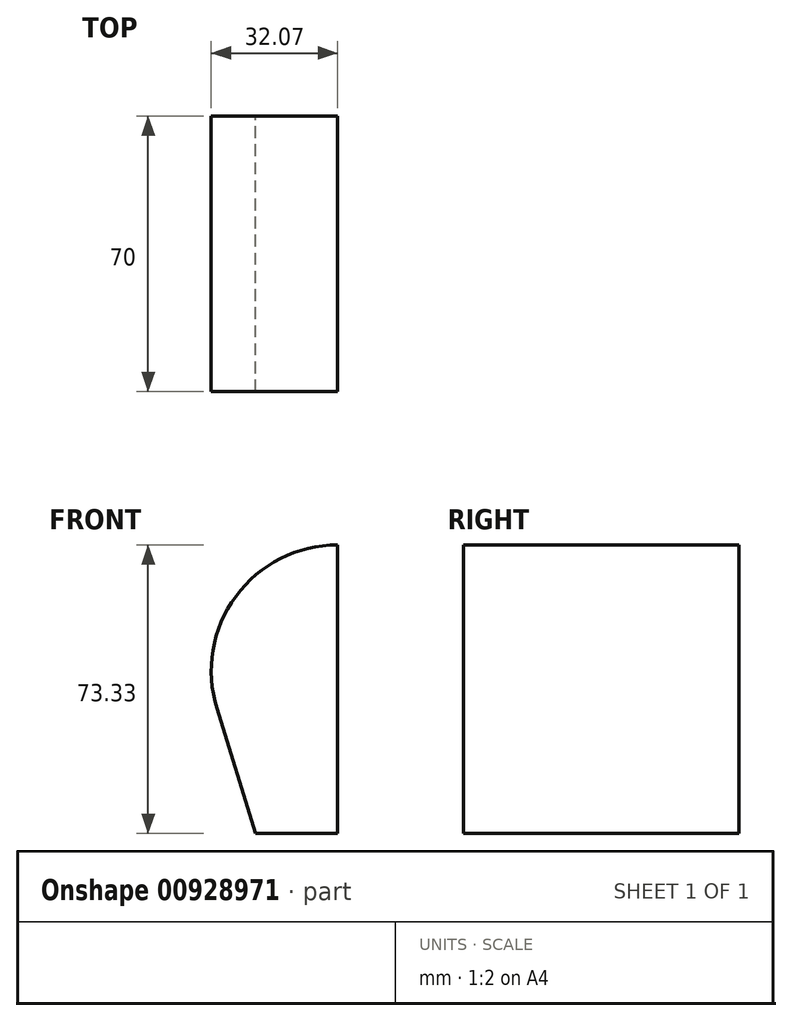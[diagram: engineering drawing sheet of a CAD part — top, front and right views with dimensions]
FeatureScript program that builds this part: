
annotation { "Feature Type Name" : "Feature", "Feature Type Description" : "" }
export const myFeature = defineFeature(function(context is Context, id is Id, definition is map)
    precondition{}
    {
        {
            var Q0;
            Q0=qCreatedBy(makeId("Front.planeOp"),FACE);
            var sketch = newSketch(context, id + "F0", { "sketchPlane" : qUnion([Q0])});
            skLineSegment(sketch, "E0", {"start": v(-16.44, -1.15) * mm, "end": v(-6.57, -32.89) * mm});
            skArc(sketch, "E1", {"start": v(14.19, 40.44) * mm, "mid": v(-11.64, 27.39) * mm, "end": v(-16.44, -1.15) * mm});
            skLineSegment(sketch, "E2", {"start": v(14.19, 40.44) * mm, "end": v(14.19, -32.89) * mm});
            skLineSegment(sketch, "E3", {"start": v(14.19, -32.89) * mm, "end": v(-6.57, -32.89) * mm});
            skSolve(sketch);
        }
        {
            var Q0;
            Q0=makeQuery(id+"F0.imprint","IMPRINT",FACE,{"disambiguationData":[TD([[makeQuery(id+"F0.imprint","IMPRINT",EDGE,{"derivedFrom":sQuery(id+"F0.wireOp",EDGE,"E0")}),1.0]])]});
            extrude(context, id + "F1", {"entities" : qUnion([Q0]), "endBound" : BoundingType.SYMMETRIC, "depth" : 70 * mm, "offsetDistance" : 25 * mm});
        }
    });
